# Revit family: 1 SOUND_LF44_Tower_Wall Bracket Mounted
name_source: partatom
category: Communication Devices
units: mm (PartAtom-declared; Revit-internal decimal feet)

## family parameters
Cut with Voids When Loaded = No
Host = Face
Maintain Annotation Orientation = No
Part Type = Normal
Room Calculation Point = No
Round Connector Dimension = Use Diameter
Shared = No

## types (1)
- LF44 with Wall Bracket
    Accessory Used = LF44 Wall Bracket
    Bandwidth = 70 Hz - 200 Hz (-6 dB preset depending)
    Category = Speaker
    Connectors = (4) NL4, each allowing for audio inputs and linking, (3) Neutrik NDL dummyPLUGs
    Construction = Finland birch plywood (phenolic glue), polyurea, clear matte salt and UV resistant coating, 316 stainless steel hardware, 3D spacer mesh fabric
    Default Elevation = 2438.40 mm
    Dimensions (HxWxD) = 452.00mm x 160.00mm x 328.00mm
    Impedance = 8Ω
    Manufacturer = 1 SOUND
    Model = LF44
    Power = 560 watts (program), 280 watts (AES)
    Rigging = Proprietary rigging elemants and fly bars -3 deg, 0 deg, +3 deg, +6 deg, +9 deg; (14) available M6 points
    Speaker Model = 1 SOUND_Tower LF44 : Tower LF44
    URL = https://www.1-sound.com
    Wall Mount Model = 1 SOUND_Tower Wall Mount : Wall Mount LF44
    Weight = 17 lbs / 7.7kg

## geometry (parser evidence)
native form markers: Sweep x19
no freeform markers — native parametric forms only
